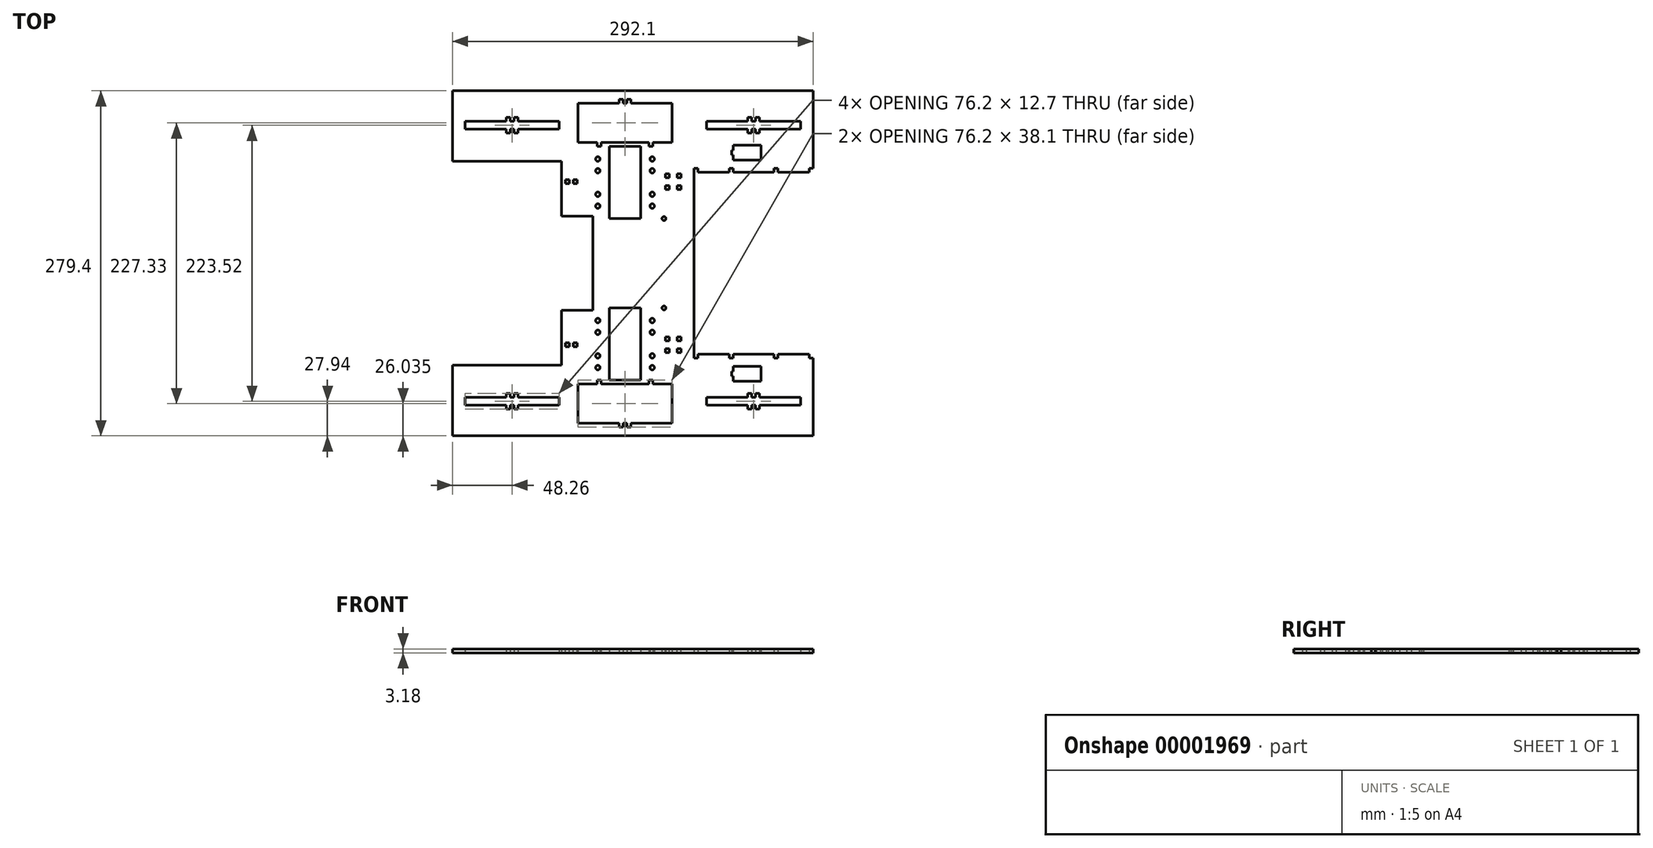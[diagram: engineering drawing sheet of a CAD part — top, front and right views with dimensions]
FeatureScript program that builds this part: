
annotation { "Feature Type Name" : "Feature", "Feature Type Description" : "" }
export const myFeature = defineFeature(function(context is Context, id is Id, definition is map)
    precondition{}
    {
        {
            var Q0;
            Q0=qCreatedBy(makeId("Top.planeOp"),FACE);
            var sketch = newSketch(context, id + "F0", { "sketchPlane" : qUnion([Q0])});
            skLineSegment(sketch, "E0.rect.bottom", {"start": v(152.4, -152.4) * mm, "end": v(-152.4, -152.4) * mm, "construction": true});
            skLineSegment(sketch, "E0.rect.top", {"start": v(152.4, 152.4) * mm, "end": v(-152.4, 152.4) * mm, "construction": true});
            skLineSegment(sketch, "E0.rect.left", {"start": v(152.4, -152.4) * mm, "end": v(152.4, 152.4) * mm, "construction": true});
            skLineSegment(sketch, "E0.rect.right", {"start": v(-152.4, -152.4) * mm, "end": v(-152.4, 152.4) * mm, "construction": true});
            skLineSegment(sketch, "E1.rect.left", {"start": v(55.88, -73.66) * mm, "end": v(55.88, 73.66) * mm});
            skLineSegment(sketch, "E2", {"start": v(152.4, 73.66) * mm, "end": v(152.4, 139.7) * mm});
            skLineSegment(sketch, "E3", {"start": v(152.4, 139.7) * mm, "end": v(-139.7, 139.7) * mm});
            skLineSegment(sketch, "E4", {"start": v(152.4, -73.66) * mm, "end": v(152.4, -139.7) * mm});
            skLineSegment(sketch, "E5", {"start": v(152.4, -139.7) * mm, "end": v(-139.7, -139.7) * mm});
            skLineSegment(sketch, "E6.rect.bottom", {"start": v(38.1, 97.8) * mm, "end": v(22.5, 97.8) * mm});
            skLineSegment(sketch, "E6.rect.top", {"start": v(38.1, 129.54) * mm, "end": v(4.76, 129.54) * mm});
            skLineSegment(sketch, "E6.rect.left", {"start": v(38.1, 97.8) * mm, "end": v(38.1, 129.54) * mm});
            skLineSegment(sketch, "E6.rect.right", {"start": v(-38.1, 97.8) * mm, "end": v(-38.1, 129.54) * mm});
            skPoint(sketch, "E6.rect.middle", {"position": v(0, 113.67) * mm});
            skLineSegment(sketch, "E7", {"start": v(55.88, 0) * mm, "end": v(-60.71, 0) * mm, "construction": true});
            skLineSegment(sketch, "E8.rect.bottom", {"start": v(12.7, 94.62) * mm, "end": v(-12.7, 94.62) * mm});
            skLineSegment(sketch, "E8.rect.top", {"start": v(12.7, 36.2) * mm, "end": v(-12.7, 36.2) * mm});
            skLineSegment(sketch, "E8.rect.left", {"start": v(12.7, 94.62) * mm, "end": v(12.7, 36.2) * mm});
            skLineSegment(sketch, "E8.rect.right", {"start": v(-12.7, 94.62) * mm, "end": v(-12.7, 36.2) * mm});
            skPoint(sketch, "E8.rect.middle", {"position": v(0, 65.4) * mm});
            skPoint(sketch, "E9.0.MirrorP", {"position": v(0, -65.4) * mm});
            skLineSegment(sketch, "E9.1.MirrorCS", {"start": v(12.7, -36.2) * mm, "end": v(-12.7, -36.2) * mm});
            skLineSegment(sketch, "E10.0.MirrorCS", {"start": v(-12.7, -94.62) * mm, "end": v(-12.7, -36.2) * mm});
            skLineSegment(sketch, "E11.0.MirrorCS", {"start": v(12.7, -94.62) * mm, "end": v(12.7, -36.2) * mm});
            skLineSegment(sketch, "E12.0.MirrorCS", {"start": v(12.7, -94.62) * mm, "end": v(-12.7, -94.62) * mm});
            skLineSegment(sketch, "E13.rect.bottom", {"start": v(136.62, -75.38) * mm, "end": v(73.12, -75.38) * mm, "construction": true});
            skLineSegment(sketch, "E13.rect.top", {"start": v(136.62, -138.88) * mm, "end": v(73.12, -138.88) * mm, "construction": true});
            skLineSegment(sketch, "E13.rect.left", {"start": v(136.62, -75.38) * mm, "end": v(136.62, -138.88) * mm, "construction": true});
            skLineSegment(sketch, "E13.rect.right", {"start": v(73.12, -75.38) * mm, "end": v(73.12, -138.88) * mm, "construction": true});
            skPoint(sketch, "E13.rect.middle", {"position": v(104.87, -107.13) * mm});
            skLineSegment(sketch, "E14", {"start": v(-139.7, 94.62) * mm, "end": v(-139.7, 139.7) * mm});
            skLineSegment(sketch, "E15.0.MirrorCS", {"start": v(-139.7, -94.62) * mm, "end": v(-139.7, -139.7) * mm});
            skLineSegment(sketch, "E16", {"start": v(-139.7, 94.62) * mm, "end": v(-139.7, 82.55) * mm});
            skLineSegment(sketch, "E17.0.MirrorCS", {"start": v(-139.7, -94.62) * mm, "end": v(-139.7, -82.55) * mm});
            skLineSegment(sketch, "E18", {"start": v(0, 65.4) * mm, "end": v(0, -65.4) * mm, "construction": true});
            skLineSegment(sketch, "E19.bottom", {"start": v(66.04, 114.94) * mm, "end": v(99.38, 114.94) * mm});
            skLineSegment(sketch, "E19.top", {"start": v(66.04, 108.59) * mm, "end": v(99.38, 108.59) * mm});
            skLineSegment(sketch, "E19.left", {"start": v(66.04, 114.94) * mm, "end": v(66.04, 108.59) * mm});
            skLineSegment(sketch, "E19.right", {"start": v(142.24, 114.94) * mm, "end": v(142.24, 108.59) * mm});
            skCircle(sketch, "E20", {"center": v(31.55, 36.2) * mm, "radius": 1.59 * mm});
            skCircle(sketch, "E21.0.MirrorC", {"center": v(31.55, -36.2) * mm, "radius": 1.59 * mm});
            skLineSegment(sketch, "E22", {"start": v(0, 65.4) * mm, "end": v(-22.02, 65.4) * mm, "construction": true});
            skLineSegment(sketch, "E23", {"start": v(-22.02, 74.93) * mm, "end": v(-22.02, 55.88) * mm, "construction": true});
            skLineSegment(sketch, "E24", {"start": v(-22.02, 74.93) * mm, "end": v(-22.02, 84.46) * mm, "construction": true});
            skLineSegment(sketch, "E25", {"start": v(-22.02, 55.88) * mm, "end": v(-22.02, 46.36) * mm, "construction": true});
            skCircle(sketch, "E26", {"center": v(-22.02, 84.46) * mm, "radius": 1.83 * mm});
            skCircle(sketch, "E27", {"center": v(-22.02, 74.93) * mm, "radius": 1.83 * mm});
            skCircle(sketch, "E28", {"center": v(-22.02, 55.88) * mm, "radius": 1.83 * mm});
            skCircle(sketch, "E29", {"center": v(-22.02, 46.36) * mm, "radius": 1.83 * mm});
            skCircle(sketch, "E30.0.MirrorC", {"center": v(22.02, 84.46) * mm, "radius": 1.83 * mm});
            skCircle(sketch, "E31.0.MirrorC", {"center": v(22.02, 74.93) * mm, "radius": 1.83 * mm});
            skCircle(sketch, "E32.0.MirrorC", {"center": v(22.02, 55.88) * mm, "radius": 1.83 * mm});
            skCircle(sketch, "E33.0.MirrorC", {"center": v(22.02, 46.36) * mm, "radius": 1.83 * mm});
            skCircle(sketch, "E34.0.MirrorC", {"center": v(22.02, -74.93) * mm, "radius": 1.83 * mm});
            skCircle(sketch, "E34.1.MirrorC", {"center": v(22.02, -46.36) * mm, "radius": 1.83 * mm});
            skCircle(sketch, "E34.2.MirrorC", {"center": v(22.02, -55.88) * mm, "radius": 1.83 * mm});
            skCircle(sketch, "E34.3.MirrorC", {"center": v(22.02, -84.46) * mm, "radius": 1.83 * mm});
            skCircle(sketch, "E35.0.MirrorC", {"center": v(-22.02, -46.36) * mm, "radius": 1.83 * mm});
            skCircle(sketch, "E36.0.MirrorC", {"center": v(-22.02, -55.88) * mm, "radius": 1.83 * mm});
            skCircle(sketch, "E37.0.MirrorC", {"center": v(-22.02, -74.93) * mm, "radius": 1.83 * mm});
            skCircle(sketch, "E38.0.MirrorC", {"center": v(-22.02, -84.46) * mm, "radius": 1.83 * mm});
            skLineSegment(sketch, "E39.0.MirrorCS", {"start": v(-89.85, 108.59) * mm, "end": v(-93.03, 108.59) * mm});
            skLineSegment(sketch, "E39.1.MirrorCS", {"start": v(-89.85, 105.4) * mm, "end": v(-86.68, 105.4) * mm});
            skLineSegment(sketch, "E39.2.MirrorCS", {"start": v(-89.85, 108.59) * mm, "end": v(-89.85, 105.4) * mm});
            skLineSegment(sketch, "E39.3.MirrorCS", {"start": v(-93.03, 108.59) * mm, "end": v(-93.03, 105.4) * mm});
            skLineSegment(sketch, "E39.4.MirrorCS", {"start": v(-93.03, 105.4) * mm, "end": v(-96.2, 105.4) * mm});
            skLineSegment(sketch, "E39.5.MirrorCS", {"start": v(-89.85, 118.1) * mm, "end": v(-86.68, 118.1) * mm});
            skLineSegment(sketch, "E39.6.MirrorCS", {"start": v(-96.2, 105.4) * mm, "end": v(-96.2, 108.59) * mm});
            skLineSegment(sketch, "E39.7.MirrorCS", {"start": v(-93.03, 118.1) * mm, "end": v(-93.03, 114.93) * mm});
            skLineSegment(sketch, "E39.8.MirrorCS", {"start": v(-89.85, 114.93) * mm, "end": v(-93.03, 114.93) * mm});
            skLineSegment(sketch, "E39.9.MirrorCS", {"start": v(-96.2, 114.93) * mm, "end": v(-96.2, 118.1) * mm});
            skLineSegment(sketch, "E39.10.MirrorCS", {"start": v(-96.2, 118.1) * mm, "end": v(-93.03, 118.1) * mm});
            skLineSegment(sketch, "E39.11.MirrorCS", {"start": v(-89.85, 114.93) * mm, "end": v(-89.85, 118.1) * mm});
            skLineSegment(sketch, "E39.12.MirrorCS", {"start": v(-86.68, 118.1) * mm, "end": v(-86.68, 114.93) * mm});
            skLineSegment(sketch, "E39.13.MirrorCS", {"start": v(-86.68, 105.4) * mm, "end": v(-86.68, 108.58) * mm});
            skLineSegment(sketch, "E39.15.MirrorCS", {"start": v(-96.2, 108.59) * mm, "end": v(-129.54, 108.59) * mm});
            skLineSegment(sketch, "E39.16.MirrorCS", {"start": v(-53.34, 114.93) * mm, "end": v(-86.68, 114.93) * mm});
            skLineSegment(sketch, "E39.17.MirrorCS", {"start": v(-96.2, 114.93) * mm, "end": v(-129.54, 114.93) * mm});
            skLineSegment(sketch, "E39.18.MirrorCS", {"start": v(-53.34, 108.59) * mm, "end": v(-86.68, 108.59) * mm});
            skLineSegment(sketch, "E39.19.MirrorCS", {"start": v(-53.34, 114.93) * mm, "end": v(-53.34, 108.58) * mm});
            skLineSegment(sketch, "E39.21.MirrorCS", {"start": v(-129.54, 114.94) * mm, "end": v(-129.54, 108.59) * mm});
            skPoint(sketch, "E40", {"position": v(104.14, 114.94) * mm});
            skLineSegment(sketch, "E41.rect.bottom", {"start": v(105.73, 114.94) * mm, "end": v(102.55, 114.94) * mm});
            skLineSegment(sketch, "E41.rect.left", {"start": v(105.73, 114.94) * mm, "end": v(105.73, 118.11) * mm});
            skLineSegment(sketch, "E41.rect.right", {"start": v(102.55, 114.94) * mm, "end": v(102.55, 118.11) * mm});
            skPoint(sketch, "E41.rect.middle", {"position": v(104.14, 116.52) * mm});
            skLineSegment(sketch, "E42", {"start": v(102.55, 118.11) * mm, "end": v(99.38, 118.11) * mm});
            skLineSegment(sketch, "E43", {"start": v(99.38, 118.11) * mm, "end": v(99.38, 114.94) * mm});
            skLineSegment(sketch, "E44", {"start": v(105.73, 118.11) * mm, "end": v(108.9, 118.11) * mm});
            skLineSegment(sketch, "E45", {"start": v(108.9, 118.11) * mm, "end": v(108.9, 114.94) * mm});
            skLineSegment(sketch, "E46.trimOffspring", {"start": v(102.55, 114.94) * mm, "end": v(105.73, 114.94) * mm});
            skLineSegment(sketch, "E47.trimOffspring", {"start": v(108.9, 114.94) * mm, "end": v(142.24, 114.94) * mm});
            skLineSegment(sketch, "E48", {"start": v(99.38, 108.59) * mm, "end": v(99.38, 105.41) * mm});
            skLineSegment(sketch, "E49", {"start": v(99.38, 105.41) * mm, "end": v(102.55, 105.41) * mm});
            skLineSegment(sketch, "E50", {"start": v(102.55, 105.41) * mm, "end": v(102.55, 108.59) * mm});
            skLineSegment(sketch, "E51", {"start": v(105.73, 108.59) * mm, "end": v(105.73, 105.41) * mm});
            skLineSegment(sketch, "E52", {"start": v(105.73, 105.41) * mm, "end": v(108.9, 105.41) * mm});
            skLineSegment(sketch, "E53", {"start": v(108.9, 105.41) * mm, "end": v(108.9, 108.59) * mm});
            skLineSegment(sketch, "E54.trimOffspring", {"start": v(102.55, 108.59) * mm, "end": v(105.73, 108.59) * mm});
            skLineSegment(sketch, "E55.trimOffspring", {"start": v(108.9, 108.59) * mm, "end": v(142.24, 108.59) * mm});
            skLineSegment(sketch, "E56.0.MirrorCS", {"start": v(102.55, -114.94) * mm, "end": v(105.73, -114.94) * mm});
            skLineSegment(sketch, "E56.1.MirrorCS", {"start": v(105.73, -114.94) * mm, "end": v(102.55, -114.94) * mm});
            skLineSegment(sketch, "E56.2.MirrorCS", {"start": v(102.55, -114.94) * mm, "end": v(102.55, -118.11) * mm});
            skLineSegment(sketch, "E56.3.MirrorCS", {"start": v(102.55, -118.11) * mm, "end": v(99.38, -118.11) * mm});
            skLineSegment(sketch, "E56.4.MirrorCS", {"start": v(108.9, -105.41) * mm, "end": v(108.9, -108.59) * mm});
            skLineSegment(sketch, "E56.5.MirrorCS", {"start": v(105.73, -118.11) * mm, "end": v(108.9, -118.11) * mm});
            skLineSegment(sketch, "E56.6.MirrorCS", {"start": v(105.73, -114.94) * mm, "end": v(105.73, -118.11) * mm});
            skLineSegment(sketch, "E56.7.MirrorCS", {"start": v(99.38, -105.41) * mm, "end": v(102.55, -105.41) * mm});
            skLineSegment(sketch, "E56.8.MirrorCS", {"start": v(102.55, -108.59) * mm, "end": v(105.73, -108.59) * mm});
            skLineSegment(sketch, "E56.9.MirrorCS", {"start": v(108.9, -118.11) * mm, "end": v(108.9, -114.94) * mm});
            skLineSegment(sketch, "E56.10.MirrorCS", {"start": v(105.73, -108.59) * mm, "end": v(105.73, -105.41) * mm});
            skLineSegment(sketch, "E56.11.MirrorCS", {"start": v(105.73, -105.41) * mm, "end": v(108.9, -105.41) * mm});
            skLineSegment(sketch, "E56.12.MirrorCS", {"start": v(99.38, -108.59) * mm, "end": v(99.38, -105.41) * mm});
            skLineSegment(sketch, "E56.13.MirrorCS", {"start": v(99.38, -118.11) * mm, "end": v(99.38, -114.94) * mm});
            skLineSegment(sketch, "E56.14.MirrorCS", {"start": v(102.55, -105.41) * mm, "end": v(102.55, -108.59) * mm});
            skLineSegment(sketch, "E56.15.MirrorCS", {"start": v(142.24, -114.94) * mm, "end": v(142.24, -108.59) * mm});
            skLineSegment(sketch, "E56.16.MirrorCS", {"start": v(108.9, -108.59) * mm, "end": v(142.24, -108.59) * mm});
            skLineSegment(sketch, "E56.17.MirrorCS", {"start": v(66.04, -114.94) * mm, "end": v(66.04, -108.59) * mm});
            skLineSegment(sketch, "E56.18.MirrorCS", {"start": v(66.04, -114.94) * mm, "end": v(99.38, -114.94) * mm});
            skLineSegment(sketch, "E56.19.MirrorCS", {"start": v(108.9, -114.94) * mm, "end": v(142.24, -114.94) * mm});
            skLineSegment(sketch, "E56.20.MirrorCS", {"start": v(66.04, -108.59) * mm, "end": v(99.38, -108.59) * mm});
            skPoint(sketch, "E56.21.MirrorP", {"position": v(104.14, -114.94) * mm});
            skPoint(sketch, "E56.22.MirrorP", {"position": v(104.14, -116.52) * mm});
            skLineSegment(sketch, "E57.rect.bottom", {"start": v(1.59, 129.54) * mm, "end": v(-1.59, 129.54) * mm});
            skLineSegment(sketch, "E57.rect.left", {"start": v(1.59, 129.54) * mm, "end": v(1.59, 132.72) * mm});
            skLineSegment(sketch, "E57.rect.right", {"start": v(-1.59, 129.54) * mm, "end": v(-1.59, 132.72) * mm});
            skPoint(sketch, "E57.rect.middle", {"position": v(0, 131.13) * mm});
            skLineSegment(sketch, "E58", {"start": v(1.59, 132.72) * mm, "end": v(4.76, 132.72) * mm});
            skLineSegment(sketch, "E59", {"start": v(4.76, 132.72) * mm, "end": v(4.76, 129.54) * mm});
            skLineSegment(sketch, "E60", {"start": v(-1.59, 132.72) * mm, "end": v(-4.76, 132.72) * mm});
            skLineSegment(sketch, "E61", {"start": v(-4.76, 132.72) * mm, "end": v(-4.76, 129.54) * mm});
            skLineSegment(sketch, "E62.trimOffspring", {"start": v(-4.76, 129.54) * mm, "end": v(-38.1, 129.54) * mm});
            skLineSegment(sketch, "E63", {"start": v(-19.33, 97.8) * mm, "end": v(-19.33, 94.62) * mm});
            skLineSegment(sketch, "E64", {"start": v(-19.33, 94.62) * mm, "end": v(-22.5, 94.62) * mm});
            skLineSegment(sketch, "E65", {"start": v(-22.5, 94.62) * mm, "end": v(-22.5, 97.8) * mm});
            skLineSegment(sketch, "E66.0.MirrorCS", {"start": v(22.5, 94.62) * mm, "end": v(22.5, 97.8) * mm});
            skLineSegment(sketch, "E66.1.MirrorCS", {"start": v(19.33, 94.62) * mm, "end": v(22.5, 94.62) * mm});
            skLineSegment(sketch, "E66.2.MirrorCS", {"start": v(19.33, 97.8) * mm, "end": v(19.33, 94.62) * mm});
            skLineSegment(sketch, "E67.trimOffspring", {"start": v(-22.5, 97.8) * mm, "end": v(-38.1, 97.8) * mm});
            skLineSegment(sketch, "E68.trimOffspring", {"start": v(19.33, 97.8) * mm, "end": v(-19.33, 97.8) * mm});
            skLineSegment(sketch, "E69.0.MirrorCS", {"start": v(1.59, -129.54) * mm, "end": v(-1.59, -129.54) * mm});
            skLineSegment(sketch, "E69.1.MirrorCS", {"start": v(1.59, -129.54) * mm, "end": v(1.59, -132.72) * mm});
            skLineSegment(sketch, "E69.2.MirrorCS", {"start": v(-1.59, -129.54) * mm, "end": v(-1.59, -132.72) * mm});
            skLineSegment(sketch, "E69.3.MirrorCS", {"start": v(1.59, -129.54) * mm, "end": v(-1.59, -129.54) * mm});
            skLineSegment(sketch, "E69.4.MirrorCS", {"start": v(-1.59, -132.72) * mm, "end": v(-4.76, -132.72) * mm});
            skLineSegment(sketch, "E69.5.MirrorCS", {"start": v(4.76, -132.72) * mm, "end": v(4.76, -129.54) * mm});
            skPoint(sketch, "E69.6.MirrorP", {"position": v(0, -131.13) * mm});
            skLineSegment(sketch, "E69.7.MirrorCS", {"start": v(1.59, -132.72) * mm, "end": v(4.76, -132.72) * mm});
            skLineSegment(sketch, "E69.8.MirrorCS", {"start": v(-4.76, -132.72) * mm, "end": v(-4.76, -129.54) * mm});
            skLineSegment(sketch, "E69.9.MirrorCS", {"start": v(-4.76, -129.54) * mm, "end": v(-38.1, -129.54) * mm});
            skPoint(sketch, "E69.10.MirrorP", {"position": v(0, -113.67) * mm});
            skLineSegment(sketch, "E69.11.MirrorCS", {"start": v(19.33, -94.62) * mm, "end": v(22.5, -94.62) * mm});
            skLineSegment(sketch, "E69.12.MirrorCS", {"start": v(19.33, -97.8) * mm, "end": v(19.33, -94.62) * mm});
            skLineSegment(sketch, "E69.13.MirrorCS", {"start": v(22.5, -94.62) * mm, "end": v(22.5, -97.8) * mm});
            skLineSegment(sketch, "E69.14.MirrorCS", {"start": v(38.1, -129.54) * mm, "end": v(4.76, -129.54) * mm});
            skLineSegment(sketch, "E69.15.MirrorCS", {"start": v(38.1, -97.8) * mm, "end": v(22.5, -97.8) * mm});
            skLineSegment(sketch, "E69.16.MirrorCS", {"start": v(19.33, -97.8) * mm, "end": v(-19.33, -97.8) * mm});
            skLineSegment(sketch, "E69.17.MirrorCS", {"start": v(38.1, -97.8) * mm, "end": v(38.1, -129.54) * mm});
            skLineSegment(sketch, "E69.18.MirrorCS", {"start": v(-19.33, -94.62) * mm, "end": v(-22.5, -94.62) * mm});
            skLineSegment(sketch, "E69.19.MirrorCS", {"start": v(-22.5, -94.62) * mm, "end": v(-22.5, -97.8) * mm});
            skLineSegment(sketch, "E69.20.MirrorCS", {"start": v(-19.33, -97.8) * mm, "end": v(-19.33, -94.62) * mm});
            skLineSegment(sketch, "E69.21.MirrorCS", {"start": v(-22.5, -97.8) * mm, "end": v(-38.1, -97.8) * mm});
            skLineSegment(sketch, "E69.22.MirrorCS", {"start": v(-38.1, -97.8) * mm, "end": v(-38.1, -129.54) * mm});
            skLineSegment(sketch, "E70", {"start": v(110.08, 83.44) * mm, "end": v(110.08, 95.63) * mm});
            skLineSegment(sketch, "E71", {"start": v(110.08, 95.63) * mm, "end": v(87.6, 95.63) * mm});
            skLineSegment(sketch, "E72", {"start": v(87.6, 95.63) * mm, "end": v(87.6, 91.44) * mm});
            skLineSegment(sketch, "E73", {"start": v(87.6, 89.53) * mm, "end": v(110.08, 89.53) * mm, "construction": true});
            skPoint(sketch, "E74", {"position": v(104.14, 89.53) * mm});
            skLineSegment(sketch, "E75", {"start": v(149.22, 73.66) * mm, "end": v(123.82, 73.66) * mm});
            skLineSegment(sketch, "E76", {"start": v(110.08, 83.44) * mm, "end": v(87.6, 83.44) * mm});
            skLineSegment(sketch, "E77", {"start": v(104.14, 89.53) * mm, "end": v(104.14, 105.41) * mm, "construction": true});
            skLineSegment(sketch, "E78", {"start": v(104.14, 89.53) * mm, "end": v(104.14, 73.66) * mm, "construction": true});
            skLineSegment(sketch, "E79", {"start": v(87.6, 91.44) * mm, "end": v(86.33, 91.44) * mm});
            skLineSegment(sketch, "E80", {"start": v(86.33, 91.44) * mm, "end": v(86.33, 89.53) * mm});
            skLineSegment(sketch, "E81", {"start": v(86.33, 87.63) * mm, "end": v(87.6, 87.63) * mm});
            skLineSegment(sketch, "E82", {"start": v(87.6, 87.63) * mm, "end": v(87.6, 83.44) * mm});
            skLineSegment(sketch, "E83", {"start": v(87.6, 91.44) * mm, "end": v(87.6, 87.63) * mm, "construction": true});
            skLineSegment(sketch, "E84", {"start": v(86.33, 89.53) * mm, "end": v(86.33, 87.63) * mm});
            skLineSegment(sketch, "E85.0.MirrorCS", {"start": v(110.08, -95.63) * mm, "end": v(87.6, -95.63) * mm});
            skLineSegment(sketch, "E86.0.MirrorCS", {"start": v(110.08, -83.44) * mm, "end": v(110.08, -95.63) * mm});
            skLineSegment(sketch, "E87.0.MirrorCS", {"start": v(110.08, -83.44) * mm, "end": v(87.6, -83.44) * mm});
            skLineSegment(sketch, "E88.0.MirrorCS", {"start": v(87.6, -87.63) * mm, "end": v(87.6, -83.44) * mm});
            skLineSegment(sketch, "E89.0.MirrorCS", {"start": v(86.33, -87.63) * mm, "end": v(87.6, -87.63) * mm});
            skLineSegment(sketch, "E90.0.MirrorCS", {"start": v(86.33, -89.53) * mm, "end": v(86.33, -87.63) * mm});
            skLineSegment(sketch, "E91.0.MirrorCS", {"start": v(86.33, -91.44) * mm, "end": v(86.33, -89.53) * mm});
            skLineSegment(sketch, "E92.0.MirrorCS", {"start": v(87.6, -91.44) * mm, "end": v(86.33, -91.44) * mm});
            skLineSegment(sketch, "E93.0.MirrorCS", {"start": v(87.6, -95.63) * mm, "end": v(87.6, -91.44) * mm});
            skLineSegment(sketch, "E94", {"start": v(55.88, 73.66) * mm, "end": v(55.88, 76.83) * mm});
            skLineSegment(sketch, "E95", {"start": v(55.88, 76.83) * mm, "end": v(59.06, 76.83) * mm});
            skLineSegment(sketch, "E96", {"start": v(59.06, 76.83) * mm, "end": v(59.06, 73.66) * mm});
            skLineSegment(sketch, "E97", {"start": v(149.22, 73.66) * mm, "end": v(149.22, 76.83) * mm});
            skLineSegment(sketch, "E98", {"start": v(149.22, 76.83) * mm, "end": v(152.4, 76.83) * mm});
            skLineSegment(sketch, "E99", {"start": v(123.82, 73.66) * mm, "end": v(123.82, 76.83) * mm});
            skLineSegment(sketch, "E100", {"start": v(123.82, 76.83) * mm, "end": v(120.65, 76.83) * mm});
            skLineSegment(sketch, "E101", {"start": v(120.65, 76.83) * mm, "end": v(120.65, 73.66) * mm});
            skLineSegment(sketch, "E102", {"start": v(84.45, 73.66) * mm, "end": v(84.45, 76.83) * mm});
            skLineSegment(sketch, "E103", {"start": v(84.45, 76.83) * mm, "end": v(87.63, 76.83) * mm});
            skLineSegment(sketch, "E104", {"start": v(87.63, 76.83) * mm, "end": v(87.63, 73.66) * mm});
            skLineSegment(sketch, "E105.trimOffspring", {"start": v(84.45, 73.66) * mm, "end": v(59.05, 73.66) * mm});
            skLineSegment(sketch, "E106.trimOffspring", {"start": v(120.65, 73.66) * mm, "end": v(87.63, 73.66) * mm});
            skLineSegment(sketch, "E107.0.MirrorCS", {"start": v(55.88, -73.66) * mm, "end": v(55.88, -76.83) * mm});
            skLineSegment(sketch, "E107.1.MirrorCS", {"start": v(55.88, -76.83) * mm, "end": v(59.06, -76.83) * mm});
            skLineSegment(sketch, "E107.2.MirrorCS", {"start": v(120.65, -76.83) * mm, "end": v(120.65, -73.66) * mm});
            skLineSegment(sketch, "E107.3.MirrorCS", {"start": v(123.83, -73.66) * mm, "end": v(123.83, -76.83) * mm});
            skLineSegment(sketch, "E107.4.MirrorCS", {"start": v(123.83, -76.83) * mm, "end": v(120.65, -76.83) * mm});
            skLineSegment(sketch, "E107.5.MirrorCS", {"start": v(59.06, -76.83) * mm, "end": v(59.06, -73.66) * mm});
            skLineSegment(sketch, "E107.6.MirrorCS", {"start": v(149.23, -73.66) * mm, "end": v(149.23, -76.83) * mm});
            skLineSegment(sketch, "E107.7.MirrorCS", {"start": v(87.63, -76.83) * mm, "end": v(87.63, -73.66) * mm});
            skLineSegment(sketch, "E107.8.MirrorCS", {"start": v(84.46, -76.83) * mm, "end": v(87.63, -76.83) * mm});
            skLineSegment(sketch, "E107.9.MirrorCS", {"start": v(84.46, -73.66) * mm, "end": v(84.46, -76.83) * mm});
            skLineSegment(sketch, "E107.10.MirrorCS", {"start": v(149.23, -76.83) * mm, "end": v(152.4, -76.83) * mm});
            skLineSegment(sketch, "E107.11.MirrorCS", {"start": v(149.23, -73.66) * mm, "end": v(123.83, -73.66) * mm});
            skLineSegment(sketch, "E107.12.MirrorCS", {"start": v(84.46, -73.66) * mm, "end": v(59.06, -73.66) * mm});
            skLineSegment(sketch, "E107.13.MirrorCS", {"start": v(120.65, -73.66) * mm, "end": v(87.63, -73.66) * mm});
            skLineSegment(sketch, "E108", {"start": v(-139.7, 82.55) * mm, "end": v(-51.59, 82.55) * mm});
            skLineSegment(sketch, "E109", {"start": v(-51.59, 82.55) * mm, "end": v(-51.59, 38.1) * mm});
            skLineSegment(sketch, "E110", {"start": v(-51.59, -82.55) * mm, "end": v(-139.7, -82.55) * mm});
            skLineSegment(sketch, "E111", {"start": v(-51.59, -38.1) * mm, "end": v(-26.19, -38.1) * mm});
            skLineSegment(sketch, "E112", {"start": v(-26.19, -38.1) * mm, "end": v(-26.19, 0) * mm});
            skLineSegment(sketch, "E113.0.MirrorCS", {"start": v(-26.19, 38.1) * mm, "end": v(-26.19, 0) * mm});
            skLineSegment(sketch, "E114.0.MirrorCS", {"start": v(-51.59, 38.1) * mm, "end": v(-26.19, 38.1) * mm});
            skLineSegment(sketch, "E115.trimOffspring", {"start": v(-51.59, -38.1) * mm, "end": v(-51.59, -82.55) * mm});
            skLineSegment(sketch, "E116.0.MirrorCS", {"start": v(-89.85, -108.59) * mm, "end": v(-89.85, -105.4) * mm});
            skLineSegment(sketch, "E116.1.MirrorCS", {"start": v(-86.68, -118.1) * mm, "end": v(-86.68, -114.93) * mm});
            skLineSegment(sketch, "E116.2.MirrorCS", {"start": v(-93.03, -105.4) * mm, "end": v(-96.2, -105.4) * mm});
            skLineSegment(sketch, "E116.3.MirrorCS", {"start": v(-89.85, -108.59) * mm, "end": v(-93.03, -108.59) * mm});
            skLineSegment(sketch, "E116.4.MirrorCS", {"start": v(-129.54, -114.94) * mm, "end": v(-129.54, -108.59) * mm});
            skLineSegment(sketch, "E116.5.MirrorCS", {"start": v(-93.03, -108.59) * mm, "end": v(-93.03, -105.4) * mm});
            skLineSegment(sketch, "E116.6.MirrorCS", {"start": v(-96.2, -114.93) * mm, "end": v(-96.2, -118.1) * mm});
            skLineSegment(sketch, "E116.7.MirrorCS", {"start": v(-96.2, -118.1) * mm, "end": v(-93.03, -118.1) * mm});
            skLineSegment(sketch, "E116.8.MirrorCS", {"start": v(-89.85, -105.4) * mm, "end": v(-86.68, -105.4) * mm});
            skLineSegment(sketch, "E116.9.MirrorCS", {"start": v(-93.03, -118.1) * mm, "end": v(-93.03, -114.93) * mm});
            skLineSegment(sketch, "E116.10.MirrorCS", {"start": v(-96.2, -105.4) * mm, "end": v(-96.2, -108.59) * mm});
            skLineSegment(sketch, "E116.11.MirrorCS", {"start": v(-86.68, -105.4) * mm, "end": v(-86.68, -108.58) * mm});
            skLineSegment(sketch, "E116.12.MirrorCS", {"start": v(-53.34, -114.93) * mm, "end": v(-53.34, -108.58) * mm});
            skLineSegment(sketch, "E116.13.MirrorCS", {"start": v(-89.85, -118.1) * mm, "end": v(-86.68, -118.1) * mm});
            skLineSegment(sketch, "E116.14.MirrorCS", {"start": v(-89.85, -114.93) * mm, "end": v(-89.85, -118.1) * mm});
            skLineSegment(sketch, "E116.15.MirrorCS", {"start": v(-89.85, -114.93) * mm, "end": v(-93.03, -114.93) * mm});
            skLineSegment(sketch, "E116.16.MirrorCS", {"start": v(-96.2, -114.93) * mm, "end": v(-129.54, -114.93) * mm});
            skLineSegment(sketch, "E116.17.MirrorCS", {"start": v(-53.34, -108.58) * mm, "end": v(-86.68, -108.59) * mm});
            skLineSegment(sketch, "E116.18.MirrorCS", {"start": v(-96.2, -108.59) * mm, "end": v(-129.54, -108.59) * mm});
            skLineSegment(sketch, "E116.19.MirrorCS", {"start": v(-53.34, -114.93) * mm, "end": v(-86.68, -114.93) * mm});
            skSolve(sketch);
        }
        {
            var Q0;
            {var subQ2=sQuery(id+"F0.wireOp",EDGE,"E3");Q0=makeQuery(id+"F0.imprint","IMPRINT",FACE,{"disambiguationData":[TD([[makeQuery(id+"F0.imprint","IMPRINT",EDGE,{"derivedFrom":subQ2}),1.0]])]});}
            extrude(context, id + "F1", {"entities" : qUnion([Q0]), "depth" : 3.17 * mm});
        }
        {
            var Q0;
            Q0=makeQuery(id+"F1.opExtrude","CAP_FACE",FACE,{"disambiguationData":[OSD([sQuery(id+"F0.wireOp",EDGE,"E2"),sQuery(id+"F0.wireOp",EDGE,"E3"),sQuery(id+"F0.wireOp",EDGE,"E4"),sQuery(id+"F0.wireOp",EDGE,"E5"),sQuery(id+"F0.wireOp",EDGE,"E6.rect.bottom"),sQuery(id+"F0.wireOp",EDGE,"E6.rect.top"),sQuery(id+"F0.wireOp",EDGE,"E6.rect.left"),sQuery(id+"F0.wireOp",EDGE,"E6.rect.right"),sQuery(id+"F0.wireOp",EDGE,"E8.rect.bottom"),sQuery(id+"F0.wireOp",EDGE,"E8.rect.top"),sQuery(id+"F0.wireOp",EDGE,"E8.rect.left"),sQuery(id+"F0.wireOp",EDGE,"E8.rect.right"),sQuery(id+"F0.wireOp",EDGE,"E9.1.MirrorCS"),sQuery(id+"F0.wireOp",EDGE,"E10.0.MirrorCS"),sQuery(id+"F0.wireOp",EDGE,"E11.0.MirrorCS"),sQuery(id+"F0.wireOp",EDGE,"E12.0.MirrorCS"),sQuery(id+"F0.wireOp",EDGE,"E14"),sQuery(id+"F0.wireOp",EDGE,"E17.0.MirrorCS"),sQuery(id+"F0.wireOp",EDGE,"E19.bottom"),sQuery(id+"F0.wireOp",EDGE,"E19.top"),sQuery(id+"F0.wireOp",EDGE,"E19.left"),sQuery(id+"F0.wireOp",EDGE,"E19.right"),sQuery(id+"F0.wireOp",EDGE,"E20"),sQuery(id+"F0.wireOp",EDGE,"E21.0.MirrorC"),sQuery(id+"F0.wireOp",EDGE,"E26"),sQuery(id+"F0.wireOp",EDGE,"E27"),sQuery(id+"F0.wireOp",EDGE,"E28"),sQuery(id+"F0.wireOp",EDGE,"E29"),sQuery(id+"F0.wireOp",EDGE,"E30.0.MirrorC"),sQuery(id+"F0.wireOp",EDGE,"E31.0.MirrorC"),sQuery(id+"F0.wireOp",EDGE,"E32.0.MirrorC"),sQuery(id+"F0.wireOp",EDGE,"E33.0.MirrorC"),sQuery(id+"F0.wireOp",EDGE,"E34.0.MirrorC"),sQuery(id+"F0.wireOp",EDGE,"E34.1.MirrorC"),sQuery(id+"F0.wireOp",EDGE,"E34.2.MirrorC"),sQuery(id+"F0.wireOp",EDGE,"E34.3.MirrorC"),sQuery(id+"F0.wireOp",EDGE,"E35.0.MirrorC"),sQuery(id+"F0.wireOp",EDGE,"E36.0.MirrorC"),sQuery(id+"F0.wireOp",EDGE,"E37.0.MirrorC"),sQuery(id+"F0.wireOp",EDGE,"E38.0.MirrorC"),sQuery(id+"F0.wireOp",EDGE,"E39.0.MirrorCS"),sQuery(id+"F0.wireOp",EDGE,"E39.1.MirrorCS"),sQuery(id+"F0.wireOp",EDGE,"E39.2.MirrorCS"),sQuery(id+"F0.wireOp",EDGE,"E39.3.MirrorCS"),sQuery(id+"F0.wireOp",EDGE,"E39.4.MirrorCS"),sQuery(id+"F0.wireOp",EDGE,"E39.5.MirrorCS"),sQuery(id+"F0.wireOp",EDGE,"E39.6.MirrorCS"),sQuery(id+"F0.wireOp",EDGE,"E39.7.MirrorCS"),sQuery(id+"F0.wireOp",EDGE,"E39.8.MirrorCS"),sQuery(id+"F0.wireOp",EDGE,"E39.9.MirrorCS"),sQuery(id+"F0.wireOp",EDGE,"E39.10.MirrorCS"),sQuery(id+"F0.wireOp",EDGE,"E39.11.MirrorCS"),sQuery(id+"F0.wireOp",EDGE,"E39.12.MirrorCS"),sQuery(id+"F0.wireOp",EDGE,"E39.13.MirrorCS"),sQuery(id+"F0.wireOp",EDGE,"E39.15.MirrorCS"),sQuery(id+"F0.wireOp",EDGE,"E39.16.MirrorCS"),sQuery(id+"F0.wireOp",EDGE,"E39.17.MirrorCS"),sQuery(id+"F0.wireOp",EDGE,"E39.18.MirrorCS"),sQuery(id+"F0.wireOp",EDGE,"E39.19.MirrorCS"),sQuery(id+"F0.wireOp",EDGE,"E39.21.MirrorCS"),sQuery(id+"F0.wireOp",EDGE,"E41.rect.left"),sQuery(id+"F0.wireOp",EDGE,"E41.rect.right"),sQuery(id+"F0.wireOp",EDGE,"E42"),sQuery(id+"F0.wireOp",EDGE,"E43"),sQuery(id+"F0.wireOp",EDGE,"E44"),sQuery(id+"F0.wireOp",EDGE,"E45"),sQuery(id+"F0.wireOp",EDGE,"E46.trimOffspring"),sQuery(id+"F0.wireOp",EDGE,"E47.trimOffspring"),sQuery(id+"F0.wireOp",EDGE,"E48"),sQuery(id+"F0.wireOp",EDGE,"E49"),sQuery(id+"F0.wireOp",EDGE,"E50"),sQuery(id+"F0.wireOp",EDGE,"E51"),sQuery(id+"F0.wireOp",EDGE,"E52"),sQuery(id+"F0.wireOp",EDGE,"E53"),sQuery(id+"F0.wireOp",EDGE,"E54.trimOffspring"),sQuery(id+"F0.wireOp",EDGE,"E55.trimOffspring"),sQuery(id+"F0.wireOp",EDGE,"E56.1.MirrorCS"),sQuery(id+"F0.wireOp",EDGE,"E56.2.MirrorCS"),sQuery(id+"F0.wireOp",EDGE,"E56.3.MirrorCS"),sQuery(id+"F0.wireOp",EDGE,"E56.4.MirrorCS"),sQuery(id+"F0.wireOp",EDGE,"E56.5.MirrorCS"),sQuery(id+"F0.wireOp",EDGE,"E56.6.MirrorCS"),sQuery(id+"F0.wireOp",EDGE,"E56.7.MirrorCS"),sQuery(id+"F0.wireOp",EDGE,"E56.8.MirrorCS"),sQuery(id+"F0.wireOp",EDGE,"E56.9.MirrorCS"),sQuery(id+"F0.wireOp",EDGE,"E56.10.MirrorCS"),sQuery(id+"F0.wireOp",EDGE,"E56.11.MirrorCS"),sQuery(id+"F0.wireOp",EDGE,"E56.12.MirrorCS"),sQuery(id+"F0.wireOp",EDGE,"E56.13.MirrorCS"),sQuery(id+"F0.wireOp",EDGE,"E56.14.MirrorCS"),sQuery(id+"F0.wireOp",EDGE,"E56.15.MirrorCS"),sQuery(id+"F0.wireOp",EDGE,"E56.16.MirrorCS"),sQuery(id+"F0.wireOp",EDGE,"E56.17.MirrorCS"),sQuery(id+"F0.wireOp",EDGE,"E56.18.MirrorCS"),sQuery(id+"F0.wireOp",EDGE,"E56.19.MirrorCS"),sQuery(id+"F0.wireOp",EDGE,"E56.20.MirrorCS"),sQuery(id+"F0.wireOp",EDGE,"E57.rect.left"),sQuery(id+"F0.wireOp",EDGE,"E57.rect.right"),sQuery(id+"F0.wireOp",EDGE,"E58"),sQuery(id+"F0.wireOp",EDGE,"E59"),sQuery(id+"F0.wireOp",EDGE,"E60"),sQuery(id+"F0.wireOp",EDGE,"E61"),sQuery(id+"F0.wireOp",EDGE,"E62.trimOffspring"),sQuery(id+"F0.wireOp",EDGE,"E57.rect.bottom"),sQuery(id+"F0.wireOp",EDGE,"E63"),sQuery(id+"F0.wireOp",EDGE,"E64"),sQuery(id+"F0.wireOp",EDGE,"E65"),sQuery(id+"F0.wireOp",EDGE,"E66.0.MirrorCS"),sQuery(id+"F0.wireOp",EDGE,"E66.1.MirrorCS"),sQuery(id+"F0.wireOp",EDGE,"E66.2.MirrorCS"),sQuery(id+"F0.wireOp",EDGE,"E67.trimOffspring"),sQuery(id+"F0.wireOp",EDGE,"E68.trimOffspring"),sQuery(id+"F0.wireOp",EDGE,"E69.1.MirrorCS"),sQuery(id+"F0.wireOp",EDGE,"E69.2.MirrorCS"),sQuery(id+"F0.wireOp",EDGE,"E69.3.MirrorCS"),sQuery(id+"F0.wireOp",EDGE,"E69.4.MirrorCS"),sQuery(id+"F0.wireOp",EDGE,"E69.5.MirrorCS"),sQuery(id+"F0.wireOp",EDGE,"E69.7.MirrorCS"),sQuery(id+"F0.wireOp",EDGE,"E69.8.MirrorCS"),sQuery(id+"F0.wireOp",EDGE,"E69.9.MirrorCS"),sQuery(id+"F0.wireOp",EDGE,"E69.11.MirrorCS"),sQuery(id+"F0.wireOp",EDGE,"E69.12.MirrorCS"),sQuery(id+"F0.wireOp",EDGE,"E69.13.MirrorCS"),sQuery(id+"F0.wireOp",EDGE,"E69.14.MirrorCS"),sQuery(id+"F0.wireOp",EDGE,"E69.15.MirrorCS"),sQuery(id+"F0.wireOp",EDGE,"E69.16.MirrorCS"),sQuery(id+"F0.wireOp",EDGE,"E69.17.MirrorCS"),sQuery(id+"F0.wireOp",EDGE,"E69.18.MirrorCS"),sQuery(id+"F0.wireOp",EDGE,"E69.19.MirrorCS"),sQuery(id+"F0.wireOp",EDGE,"E69.20.MirrorCS"),sQuery(id+"F0.wireOp",EDGE,"E69.21.MirrorCS"),sQuery(id+"F0.wireOp",EDGE,"E69.22.MirrorCS"),sQuery(id+"F0.wireOp",EDGE,"E70"),sQuery(id+"F0.wireOp",EDGE,"E71"),sQuery(id+"F0.wireOp",EDGE,"E72"),sQuery(id+"F0.wireOp",EDGE,"E75"),sQuery(id+"F0.wireOp",EDGE,"E76"),sQuery(id+"F0.wireOp",EDGE,"E79"),sQuery(id+"F0.wireOp",EDGE,"E80"),sQuery(id+"F0.wireOp",EDGE,"E81"),sQuery(id+"F0.wireOp",EDGE,"E82"),sQuery(id+"F0.wireOp",EDGE,"E84"),sQuery(id+"F0.wireOp",EDGE,"E85.0.MirrorCS"),sQuery(id+"F0.wireOp",EDGE,"E86.0.MirrorCS"),sQuery(id+"F0.wireOp",EDGE,"E87.0.MirrorCS"),sQuery(id+"F0.wireOp",EDGE,"E88.0.MirrorCS"),sQuery(id+"F0.wireOp",EDGE,"E89.0.MirrorCS"),sQuery(id+"F0.wireOp",EDGE,"E90.0.MirrorCS"),sQuery(id+"F0.wireOp",EDGE,"E91.0.MirrorCS"),sQuery(id+"F0.wireOp",EDGE,"E92.0.MirrorCS"),sQuery(id+"F0.wireOp",EDGE,"E93.0.MirrorCS"),sQuery(id+"F0.wireOp",EDGE,"E95"),sQuery(id+"F0.wireOp",EDGE,"E96"),sQuery(id+"F0.wireOp",EDGE,"E97"),sQuery(id+"F0.wireOp",EDGE,"E98"),sQuery(id+"F0.wireOp",EDGE,"E99"),sQuery(id+"F0.wireOp",EDGE,"E100"),sQuery(id+"F0.wireOp",EDGE,"E101"),sQuery(id+"F0.wireOp",EDGE,"E102"),sQuery(id+"F0.wireOp",EDGE,"E103"),sQuery(id+"F0.wireOp",EDGE,"E104"),sQuery(id+"F0.wireOp",EDGE,"E105.trimOffspring"),sQuery(id+"F0.wireOp",EDGE,"E106.trimOffspring"),sQuery(id+"F0.wireOp",EDGE,"E107.0.MirrorCS"),sQuery(id+"F0.wireOp",EDGE,"E107.1.MirrorCS"),sQuery(id+"F0.wireOp",EDGE,"E107.2.MirrorCS"),sQuery(id+"F0.wireOp",EDGE,"E107.3.MirrorCS"),sQuery(id+"F0.wireOp",EDGE,"E107.4.MirrorCS"),sQuery(id+"F0.wireOp",EDGE,"E107.5.MirrorCS"),sQuery(id+"F0.wireOp",EDGE,"E107.6.MirrorCS"),sQuery(id+"F0.wireOp",EDGE,"E107.7.MirrorCS"),sQuery(id+"F0.wireOp",EDGE,"E107.8.MirrorCS"),sQuery(id+"F0.wireOp",EDGE,"E107.9.MirrorCS"),sQuery(id+"F0.wireOp",EDGE,"E107.10.MirrorCS"),sQuery(id+"F0.wireOp",EDGE,"E107.11.MirrorCS"),sQuery(id+"F0.wireOp",EDGE,"E107.12.MirrorCS"),sQuery(id+"F0.wireOp",EDGE,"E107.13.MirrorCS"),sQuery(id+"F0.wireOp",EDGE,"E108"),sQuery(id+"F0.wireOp",EDGE,"E109"),sQuery(id+"F0.wireOp",EDGE,"E110"),sQuery(id+"F0.wireOp",EDGE,"E111"),sQuery(id+"F0.wireOp",EDGE,"E113.0.MirrorCS"),sQuery(id+"F0.wireOp",EDGE,"E114.0.MirrorCS"),sQuery(id+"F0.wireOp",EDGE,"E115.trimOffspring"),sQuery(id+"F0.wireOp",EDGE,"E116.0.MirrorCS"),sQuery(id+"F0.wireOp",EDGE,"E116.1.MirrorCS"),sQuery(id+"F0.wireOp",EDGE,"E116.2.MirrorCS"),sQuery(id+"F0.wireOp",EDGE,"E116.3.MirrorCS"),sQuery(id+"F0.wireOp",EDGE,"E116.4.MirrorCS"),sQuery(id+"F0.wireOp",EDGE,"E116.5.MirrorCS"),sQuery(id+"F0.wireOp",EDGE,"E116.6.MirrorCS"),sQuery(id+"F0.wireOp",EDGE,"E116.7.MirrorCS"),sQuery(id+"F0.wireOp",EDGE,"E116.8.MirrorCS"),sQuery(id+"F0.wireOp",EDGE,"E116.9.MirrorCS"),sQuery(id+"F0.wireOp",EDGE,"E116.10.MirrorCS"),sQuery(id+"F0.wireOp",EDGE,"E116.11.MirrorCS"),sQuery(id+"F0.wireOp",EDGE,"E116.12.MirrorCS"),sQuery(id+"F0.wireOp",EDGE,"E116.13.MirrorCS"),sQuery(id+"F0.wireOp",EDGE,"E116.14.MirrorCS"),sQuery(id+"F0.wireOp",EDGE,"E116.15.MirrorCS"),sQuery(id+"F0.wireOp",EDGE,"E116.16.MirrorCS"),sQuery(id+"F0.wireOp",EDGE,"E116.17.MirrorCS"),sQuery(id+"F0.wireOp",EDGE,"E116.18.MirrorCS"),sQuery(id+"F0.wireOp",EDGE,"E116.19.MirrorCS")])],"isStart":false});
            var sketch = newSketch(context, id + "F2", { "sketchPlane" : qUnion([Q0])});
            skPoint(sketch, "E117", {"position": v(39.05, 66.04) * mm});
            skLineSegment(sketch, "E118.rect.bottom", {"start": v(42.23, 62.87) * mm, "end": v(35.88, 62.87) * mm, "construction": true});
            skLineSegment(sketch, "E118.rect.top", {"start": v(42.23, 69.22) * mm, "end": v(35.88, 69.22) * mm, "construction": true});
            skLineSegment(sketch, "E118.rect.left", {"start": v(42.23, 62.87) * mm, "end": v(42.23, 69.22) * mm, "construction": true});
            skLineSegment(sketch, "E118.rect.right", {"start": v(35.88, 62.87) * mm, "end": v(35.88, 69.22) * mm, "construction": true});
            skLineSegment(sketch, "E119.bottom", {"start": v(42.23, 69.22) * mm, "end": v(45.4, 69.22) * mm});
            skLineSegment(sketch, "E119.top", {"start": v(42.23, 72.4) * mm, "end": v(45.4, 72.4) * mm});
            skLineSegment(sketch, "E119.left", {"start": v(42.23, 69.22) * mm, "end": v(42.23, 72.4) * mm});
            skLineSegment(sketch, "E119.right", {"start": v(45.4, 69.22) * mm, "end": v(45.4, 72.4) * mm});
            skLineSegment(sketch, "E120", {"start": v(35.88, 66.04) * mm, "end": v(42.23, 66.04) * mm, "construction": true});
            skLineSegment(sketch, "E121", {"start": v(39.05, 69.22) * mm, "end": v(39.05, 62.87) * mm, "construction": true});
            skLineSegment(sketch, "E122.0.MirrorCS", {"start": v(35.88, 69.22) * mm, "end": v(32.7, 69.22) * mm});
            skLineSegment(sketch, "E123.0.MirrorCS", {"start": v(32.7, 69.22) * mm, "end": v(32.7, 72.4) * mm});
            skLineSegment(sketch, "E124.0.MirrorCS", {"start": v(35.88, 72.4) * mm, "end": v(32.7, 72.4) * mm});
            skLineSegment(sketch, "E125.0.MirrorCS", {"start": v(35.88, 69.22) * mm, "end": v(35.88, 72.4) * mm});
            skLineSegment(sketch, "E126.0.MirrorCS", {"start": v(32.7, 62.87) * mm, "end": v(32.7, 59.7) * mm});
            skLineSegment(sketch, "E127.0.MirrorCS", {"start": v(35.88, 59.7) * mm, "end": v(32.7, 59.7) * mm});
            skLineSegment(sketch, "E128.0.MirrorCS", {"start": v(35.88, 62.87) * mm, "end": v(35.88, 59.7) * mm});
            skLineSegment(sketch, "E129.0.MirrorCS", {"start": v(42.23, 62.87) * mm, "end": v(45.4, 62.87) * mm});
            skLineSegment(sketch, "E130.0.MirrorCS", {"start": v(42.23, 62.87) * mm, "end": v(42.23, 59.7) * mm});
            skLineSegment(sketch, "E131.0.MirrorCS", {"start": v(42.23, 59.7) * mm, "end": v(45.4, 59.7) * mm});
            skLineSegment(sketch, "E132.0.MirrorCS", {"start": v(45.4, 62.87) * mm, "end": v(45.4, 59.7) * mm});
            skLineSegment(sketch, "E133.0.MirrorCS", {"start": v(35.88, 62.87) * mm, "end": v(32.7, 62.87) * mm});
            skLineSegment(sketch, "E134.0.MirrorCS", {"start": v(42.23, -69.21) * mm, "end": v(45.4, -69.21) * mm});
            skLineSegment(sketch, "E135.0.MirrorCS", {"start": v(45.4, -69.21) * mm, "end": v(45.4, -72.39) * mm});
            skLineSegment(sketch, "E136.0.MirrorCS", {"start": v(42.23, -72.39) * mm, "end": v(45.4, -72.39) * mm});
            skLineSegment(sketch, "E137.0.MirrorCS", {"start": v(42.23, -69.21) * mm, "end": v(42.23, -72.39) * mm});
            skLineSegment(sketch, "E138.0.MirrorCS", {"start": v(35.88, -69.21) * mm, "end": v(35.88, -72.39) * mm});
            skLineSegment(sketch, "E139.0.MirrorCS", {"start": v(35.88, -72.39) * mm, "end": v(32.7, -72.39) * mm});
            skLineSegment(sketch, "E140.0.MirrorCS", {"start": v(35.88, -69.21) * mm, "end": v(32.7, -69.21) * mm});
            skLineSegment(sketch, "E141.0.MirrorCS", {"start": v(32.7, -69.21) * mm, "end": v(32.7, -72.39) * mm});
            skLineSegment(sketch, "E142.0.MirrorCS", {"start": v(35.88, -62.86) * mm, "end": v(32.7, -62.86) * mm});
            skLineSegment(sketch, "E143.0.MirrorCS", {"start": v(35.88, -62.86) * mm, "end": v(35.88, -59.69) * mm});
            skLineSegment(sketch, "E144.0.MirrorCS", {"start": v(35.88, -59.69) * mm, "end": v(32.7, -59.69) * mm});
            skLineSegment(sketch, "E145.0.MirrorCS", {"start": v(32.7, -62.86) * mm, "end": v(32.7, -59.69) * mm});
            skLineSegment(sketch, "E146.0.MirrorCS", {"start": v(42.23, -62.86) * mm, "end": v(45.4, -62.86) * mm});
            skLineSegment(sketch, "E147.0.MirrorCS", {"start": v(42.23, -62.86) * mm, "end": v(42.23, -59.69) * mm});
            skLineSegment(sketch, "E148.0.MirrorCS", {"start": v(42.23, -59.69) * mm, "end": v(45.4, -59.69) * mm});
            skLineSegment(sketch, "E149.0.MirrorCS", {"start": v(45.4, -62.86) * mm, "end": v(45.4, -59.69) * mm});
            skPoint(sketch, "E150", {"position": v(39.05, 27.94) * mm});
            skLineSegment(sketch, "E151.rect.bottom", {"start": v(40.64, 29.65) * mm, "end": v(37.46, 29.65) * mm, "construction": true});
            skLineSegment(sketch, "E151.rect.top", {"start": v(40.64, 32.83) * mm, "end": v(37.46, 32.83) * mm, "construction": true});
            skLineSegment(sketch, "E151.rect.left", {"start": v(40.64, 29.65) * mm, "end": v(40.64, 32.83) * mm, "construction": true});
            skLineSegment(sketch, "E151.rect.right", {"start": v(37.46, 29.65) * mm, "end": v(37.46, 32.83) * mm, "construction": true});
            skPoint(sketch, "E151.rect.middle", {"position": v(39.05, 31.24) * mm});
            skLineSegment(sketch, "E152.rect.bottom", {"start": v(40.64, 23.05) * mm, "end": v(37.46, 23.05) * mm, "construction": true});
            skLineSegment(sketch, "E152.rect.top", {"start": v(40.64, 26.23) * mm, "end": v(37.46, 26.23) * mm, "construction": true});
            skLineSegment(sketch, "E152.rect.left", {"start": v(40.64, 23.05) * mm, "end": v(40.64, 26.23) * mm, "construction": true});
            skLineSegment(sketch, "E152.rect.right", {"start": v(37.46, 23.05) * mm, "end": v(37.46, 26.23) * mm, "construction": true});
            skPoint(sketch, "E152.rect.middle", {"position": v(39.05, 24.64) * mm});
            skLineSegment(sketch, "E153.0.MirrorCS", {"start": v(40.64, -26.23) * mm, "end": v(37.46, -26.23) * mm, "construction": true});
            skLineSegment(sketch, "E153.1.MirrorCS", {"start": v(40.64, -32.83) * mm, "end": v(37.46, -32.83) * mm, "construction": true});
            skLineSegment(sketch, "E153.2.MirrorCS", {"start": v(40.64, -29.65) * mm, "end": v(40.64, -32.83) * mm, "construction": true});
            skPoint(sketch, "E153.3.MirrorP", {"position": v(39.05, -31.24) * mm});
            skLineSegment(sketch, "E153.4.MirrorCS", {"start": v(37.46, -29.65) * mm, "end": v(37.46, -32.83) * mm, "construction": true});
            skLineSegment(sketch, "E153.5.MirrorCS", {"start": v(40.64, -29.65) * mm, "end": v(37.46, -29.65) * mm, "construction": true});
            skPoint(sketch, "E153.6.MirrorP", {"position": v(39.05, -27.94) * mm});
            skLineSegment(sketch, "E153.7.MirrorCS", {"start": v(40.64, -23.05) * mm, "end": v(40.64, -26.23) * mm, "construction": true});
            skPoint(sketch, "E153.8.MirrorP", {"position": v(39.05, -24.64) * mm});
            skLineSegment(sketch, "E153.9.MirrorCS", {"start": v(40.64, -23.05) * mm, "end": v(37.46, -23.05) * mm, "construction": true});
            skLineSegment(sketch, "E153.10.MirrorCS", {"start": v(37.46, -23.05) * mm, "end": v(37.46, -26.23) * mm, "construction": true});
            skPoint(sketch, "E154", {"position": v(-43.5, 66.04) * mm});
            skLineSegment(sketch, "E155.rect.bottom", {"start": v(-38.6, 64.45) * mm, "end": v(-41.78, 64.45) * mm});
            skLineSegment(sketch, "E155.rect.top", {"start": v(-38.6, 67.63) * mm, "end": v(-41.78, 67.63) * mm});
            skLineSegment(sketch, "E155.rect.left", {"start": v(-38.6, 64.45) * mm, "end": v(-38.6, 67.63) * mm});
            skLineSegment(sketch, "E155.rect.right", {"start": v(-41.78, 64.45) * mm, "end": v(-41.78, 67.63) * mm});
            skPoint(sketch, "E155.rect.middle", {"position": v(-40.2, 66.04) * mm});
            skLineSegment(sketch, "E156.rect.bottom", {"start": v(-45.21, 64.45) * mm, "end": v(-48.39, 64.45) * mm});
            skLineSegment(sketch, "E156.rect.top", {"start": v(-45.21, 67.63) * mm, "end": v(-48.39, 67.63) * mm});
            skLineSegment(sketch, "E156.rect.left", {"start": v(-45.21, 64.45) * mm, "end": v(-45.21, 67.63) * mm});
            skLineSegment(sketch, "E156.rect.right", {"start": v(-48.39, 64.45) * mm, "end": v(-48.39, 67.63) * mm});
            skPoint(sketch, "E156.rect.middle", {"position": v(-46.8, 66.04) * mm});
            skLineSegment(sketch, "E157.0.MirrorCS", {"start": v(-45.21, -67.63) * mm, "end": v(-48.39, -67.63) * mm});
            skPoint(sketch, "E157.1.MirrorP", {"position": v(-46.8, -66.04) * mm});
            skLineSegment(sketch, "E157.2.MirrorCS", {"start": v(-45.21, -64.45) * mm, "end": v(-45.21, -67.63) * mm});
            skPoint(sketch, "E157.3.MirrorP", {"position": v(-43.5, -66.04) * mm});
            skLineSegment(sketch, "E157.4.MirrorCS", {"start": v(-48.39, -64.45) * mm, "end": v(-48.39, -67.63) * mm});
            skLineSegment(sketch, "E157.5.MirrorCS", {"start": v(-45.21, -64.45) * mm, "end": v(-48.39, -64.45) * mm});
            skLineSegment(sketch, "E157.6.MirrorCS", {"start": v(-38.6, -67.63) * mm, "end": v(-41.78, -67.63) * mm});
            skLineSegment(sketch, "E157.7.MirrorCS", {"start": v(-41.78, -64.45) * mm, "end": v(-41.78, -67.63) * mm});
            skPoint(sketch, "E157.8.MirrorP", {"position": v(-40.2, -66.04) * mm});
            skLineSegment(sketch, "E157.9.MirrorCS", {"start": v(-38.6, -64.45) * mm, "end": v(-41.78, -64.45) * mm});
            skLineSegment(sketch, "E157.10.MirrorCS", {"start": v(-38.6, -64.45) * mm, "end": v(-38.6, -67.63) * mm});
            skSolve(sketch);
        }
        {
            var Q0;
            {Q0=qUnion([makeQuery(id+"F2.imprint","IMPRINT",FACE,{"disambiguationData":[TD([[makeQuery(id+"F2.imprint","IMPRINT",EDGE,{"derivedFrom":sQuery(id+"F2.wireOp",EDGE,"E119.bottom")}),1.0]])]}),makeQuery(id+"F2.imprint","IMPRINT",FACE,{"disambiguationData":[TD([[makeQuery(id+"F2.imprint","IMPRINT",EDGE,{"derivedFrom":sQuery(id+"F2.wireOp",EDGE,"E122.0.MirrorCS")}),-1.0]])]}),makeQuery(id+"F2.imprint","IMPRINT",FACE,{"disambiguationData":[TD([[makeQuery(id+"F2.imprint","IMPRINT",EDGE,{"derivedFrom":sQuery(id+"F2.wireOp",EDGE,"E126.0.MirrorCS")}),1.0]])]}),makeQuery(id+"F2.imprint","IMPRINT",FACE,{"disambiguationData":[TD([[makeQuery(id+"F2.imprint","IMPRINT",EDGE,{"derivedFrom":sQuery(id+"F2.wireOp",EDGE,"E129.0.MirrorCS")}),-1.0]])]}),makeQuery(id+"F2.imprint","IMPRINT",FACE,{"disambiguationData":[TD([[makeQuery(id+"F2.imprint","IMPRINT",EDGE,{"derivedFrom":sQuery(id+"F2.wireOp",EDGE,"E134.0.MirrorCS")}),-1.0]])]}),makeQuery(id+"F2.imprint","IMPRINT",FACE,{"disambiguationData":[TD([[makeQuery(id+"F2.imprint","IMPRINT",EDGE,{"derivedFrom":sQuery(id+"F2.wireOp",EDGE,"E138.0.MirrorCS")}),-1.0]])]}),makeQuery(id+"F2.imprint","IMPRINT",FACE,{"disambiguationData":[TD([[makeQuery(id+"F2.imprint","IMPRINT",EDGE,{"derivedFrom":sQuery(id+"F2.wireOp",EDGE,"E142.0.MirrorCS")}),-1.0]])]}),makeQuery(id+"F2.imprint","IMPRINT",FACE,{"disambiguationData":[TD([[makeQuery(id+"F2.imprint","IMPRINT",EDGE,{"derivedFrom":sQuery(id+"F2.wireOp",EDGE,"E146.0.MirrorCS")}),1.0]])]}),makeQuery(id+"F2.imprint","IMPRINT",FACE,{"disambiguationData":[TD([[makeQuery(id+"F2.imprint","IMPRINT",EDGE,{"derivedFrom":sQuery(id+"F2.wireOp",EDGE,"E155.rect.bottom")}),-1.0]])]}),makeQuery(id+"F2.imprint","IMPRINT",FACE,{"disambiguationData":[TD([[makeQuery(id+"F2.imprint","IMPRINT",EDGE,{"derivedFrom":sQuery(id+"F2.wireOp",EDGE,"E156.rect.bottom")}),-1.0]])]}),makeQuery(id+"F2.imprint","IMPRINT",FACE,{"disambiguationData":[TD([[makeQuery(id+"F2.imprint","IMPRINT",EDGE,{"derivedFrom":sQuery(id+"F2.wireOp",EDGE,"E157.0.MirrorCS")}),-1.0]])]}),makeQuery(id+"F2.imprint","IMPRINT",FACE,{"disambiguationData":[TD([[makeQuery(id+"F2.imprint","IMPRINT",EDGE,{"derivedFrom":sQuery(id+"F2.wireOp",EDGE,"E157.6.MirrorCS")}),-1.0]])]})]);}
            var Q1;
            Q1=makeQuery(id+"F1.opExtrude","CAP_FACE",FACE,{"disambiguationData":[OSD([sQuery(id+"F0.wireOp",EDGE,"E2"),sQuery(id+"F0.wireOp",EDGE,"E3"),sQuery(id+"F0.wireOp",EDGE,"E4"),sQuery(id+"F0.wireOp",EDGE,"E5"),sQuery(id+"F0.wireOp",EDGE,"E6.rect.bottom"),sQuery(id+"F0.wireOp",EDGE,"E6.rect.top"),sQuery(id+"F0.wireOp",EDGE,"E6.rect.left"),sQuery(id+"F0.wireOp",EDGE,"E6.rect.right"),sQuery(id+"F0.wireOp",EDGE,"E8.rect.bottom"),sQuery(id+"F0.wireOp",EDGE,"E8.rect.top"),sQuery(id+"F0.wireOp",EDGE,"E8.rect.left"),sQuery(id+"F0.wireOp",EDGE,"E8.rect.right"),sQuery(id+"F0.wireOp",EDGE,"E9.1.MirrorCS"),sQuery(id+"F0.wireOp",EDGE,"E10.0.MirrorCS"),sQuery(id+"F0.wireOp",EDGE,"E11.0.MirrorCS"),sQuery(id+"F0.wireOp",EDGE,"E12.0.MirrorCS"),sQuery(id+"F0.wireOp",EDGE,"E14"),sQuery(id+"F0.wireOp",EDGE,"E17.0.MirrorCS"),sQuery(id+"F0.wireOp",EDGE,"E19.bottom"),sQuery(id+"F0.wireOp",EDGE,"E19.top"),sQuery(id+"F0.wireOp",EDGE,"E19.left"),sQuery(id+"F0.wireOp",EDGE,"E19.right"),sQuery(id+"F0.wireOp",EDGE,"E20"),sQuery(id+"F0.wireOp",EDGE,"E21.0.MirrorC"),sQuery(id+"F0.wireOp",EDGE,"E26"),sQuery(id+"F0.wireOp",EDGE,"E27"),sQuery(id+"F0.wireOp",EDGE,"E28"),sQuery(id+"F0.wireOp",EDGE,"E29"),sQuery(id+"F0.wireOp",EDGE,"E30.0.MirrorC"),sQuery(id+"F0.wireOp",EDGE,"E31.0.MirrorC"),sQuery(id+"F0.wireOp",EDGE,"E32.0.MirrorC"),sQuery(id+"F0.wireOp",EDGE,"E33.0.MirrorC"),sQuery(id+"F0.wireOp",EDGE,"E34.0.MirrorC"),sQuery(id+"F0.wireOp",EDGE,"E34.1.MirrorC"),sQuery(id+"F0.wireOp",EDGE,"E34.2.MirrorC"),sQuery(id+"F0.wireOp",EDGE,"E34.3.MirrorC"),sQuery(id+"F0.wireOp",EDGE,"E35.0.MirrorC"),sQuery(id+"F0.wireOp",EDGE,"E36.0.MirrorC"),sQuery(id+"F0.wireOp",EDGE,"E37.0.MirrorC"),sQuery(id+"F0.wireOp",EDGE,"E38.0.MirrorC"),sQuery(id+"F0.wireOp",EDGE,"E39.0.MirrorCS"),sQuery(id+"F0.wireOp",EDGE,"E39.1.MirrorCS"),sQuery(id+"F0.wireOp",EDGE,"E39.2.MirrorCS"),sQuery(id+"F0.wireOp",EDGE,"E39.3.MirrorCS"),sQuery(id+"F0.wireOp",EDGE,"E39.4.MirrorCS"),sQuery(id+"F0.wireOp",EDGE,"E39.5.MirrorCS"),sQuery(id+"F0.wireOp",EDGE,"E39.6.MirrorCS"),sQuery(id+"F0.wireOp",EDGE,"E39.7.MirrorCS"),sQuery(id+"F0.wireOp",EDGE,"E39.8.MirrorCS"),sQuery(id+"F0.wireOp",EDGE,"E39.9.MirrorCS"),sQuery(id+"F0.wireOp",EDGE,"E39.10.MirrorCS"),sQuery(id+"F0.wireOp",EDGE,"E39.11.MirrorCS"),sQuery(id+"F0.wireOp",EDGE,"E39.12.MirrorCS"),sQuery(id+"F0.wireOp",EDGE,"E39.13.MirrorCS"),sQuery(id+"F0.wireOp",EDGE,"E39.15.MirrorCS"),sQuery(id+"F0.wireOp",EDGE,"E39.16.MirrorCS"),sQuery(id+"F0.wireOp",EDGE,"E39.17.MirrorCS"),sQuery(id+"F0.wireOp",EDGE,"E39.18.MirrorCS"),sQuery(id+"F0.wireOp",EDGE,"E39.19.MirrorCS"),sQuery(id+"F0.wireOp",EDGE,"E39.21.MirrorCS"),sQuery(id+"F0.wireOp",EDGE,"E41.rect.left"),sQuery(id+"F0.wireOp",EDGE,"E41.rect.right"),sQuery(id+"F0.wireOp",EDGE,"E42"),sQuery(id+"F0.wireOp",EDGE,"E43"),sQuery(id+"F0.wireOp",EDGE,"E44"),sQuery(id+"F0.wireOp",EDGE,"E45"),sQuery(id+"F0.wireOp",EDGE,"E46.trimOffspring"),sQuery(id+"F0.wireOp",EDGE,"E47.trimOffspring"),sQuery(id+"F0.wireOp",EDGE,"E48"),sQuery(id+"F0.wireOp",EDGE,"E49"),sQuery(id+"F0.wireOp",EDGE,"E50"),sQuery(id+"F0.wireOp",EDGE,"E51"),sQuery(id+"F0.wireOp",EDGE,"E52"),sQuery(id+"F0.wireOp",EDGE,"E53"),sQuery(id+"F0.wireOp",EDGE,"E54.trimOffspring"),sQuery(id+"F0.wireOp",EDGE,"E55.trimOffspring"),sQuery(id+"F0.wireOp",EDGE,"E56.1.MirrorCS"),sQuery(id+"F0.wireOp",EDGE,"E56.2.MirrorCS"),sQuery(id+"F0.wireOp",EDGE,"E56.3.MirrorCS"),sQuery(id+"F0.wireOp",EDGE,"E56.4.MirrorCS"),sQuery(id+"F0.wireOp",EDGE,"E56.5.MirrorCS"),sQuery(id+"F0.wireOp",EDGE,"E56.6.MirrorCS"),sQuery(id+"F0.wireOp",EDGE,"E56.7.MirrorCS"),sQuery(id+"F0.wireOp",EDGE,"E56.8.MirrorCS"),sQuery(id+"F0.wireOp",EDGE,"E56.9.MirrorCS"),sQuery(id+"F0.wireOp",EDGE,"E56.10.MirrorCS"),sQuery(id+"F0.wireOp",EDGE,"E56.11.MirrorCS"),sQuery(id+"F0.wireOp",EDGE,"E56.12.MirrorCS"),sQuery(id+"F0.wireOp",EDGE,"E56.13.MirrorCS"),sQuery(id+"F0.wireOp",EDGE,"E56.14.MirrorCS"),sQuery(id+"F0.wireOp",EDGE,"E56.15.MirrorCS"),sQuery(id+"F0.wireOp",EDGE,"E56.16.MirrorCS"),sQuery(id+"F0.wireOp",EDGE,"E56.17.MirrorCS"),sQuery(id+"F0.wireOp",EDGE,"E56.18.MirrorCS"),sQuery(id+"F0.wireOp",EDGE,"E56.19.MirrorCS"),sQuery(id+"F0.wireOp",EDGE,"E56.20.MirrorCS"),sQuery(id+"F0.wireOp",EDGE,"E57.rect.left"),sQuery(id+"F0.wireOp",EDGE,"E57.rect.right"),sQuery(id+"F0.wireOp",EDGE,"E58"),sQuery(id+"F0.wireOp",EDGE,"E59"),sQuery(id+"F0.wireOp",EDGE,"E60"),sQuery(id+"F0.wireOp",EDGE,"E61"),sQuery(id+"F0.wireOp",EDGE,"E62.trimOffspring"),sQuery(id+"F0.wireOp",EDGE,"E57.rect.bottom"),sQuery(id+"F0.wireOp",EDGE,"E63"),sQuery(id+"F0.wireOp",EDGE,"E64"),sQuery(id+"F0.wireOp",EDGE,"E65"),sQuery(id+"F0.wireOp",EDGE,"E66.0.MirrorCS"),sQuery(id+"F0.wireOp",EDGE,"E66.1.MirrorCS"),sQuery(id+"F0.wireOp",EDGE,"E66.2.MirrorCS"),sQuery(id+"F0.wireOp",EDGE,"E67.trimOffspring"),sQuery(id+"F0.wireOp",EDGE,"E68.trimOffspring"),sQuery(id+"F0.wireOp",EDGE,"E69.1.MirrorCS"),sQuery(id+"F0.wireOp",EDGE,"E69.2.MirrorCS"),sQuery(id+"F0.wireOp",EDGE,"E69.3.MirrorCS"),sQuery(id+"F0.wireOp",EDGE,"E69.4.MirrorCS"),sQuery(id+"F0.wireOp",EDGE,"E69.5.MirrorCS"),sQuery(id+"F0.wireOp",EDGE,"E69.7.MirrorCS"),sQuery(id+"F0.wireOp",EDGE,"E69.8.MirrorCS"),sQuery(id+"F0.wireOp",EDGE,"E69.9.MirrorCS"),sQuery(id+"F0.wireOp",EDGE,"E69.11.MirrorCS"),sQuery(id+"F0.wireOp",EDGE,"E69.12.MirrorCS"),sQuery(id+"F0.wireOp",EDGE,"E69.13.MirrorCS"),sQuery(id+"F0.wireOp",EDGE,"E69.14.MirrorCS"),sQuery(id+"F0.wireOp",EDGE,"E69.15.MirrorCS"),sQuery(id+"F0.wireOp",EDGE,"E69.16.MirrorCS"),sQuery(id+"F0.wireOp",EDGE,"E69.17.MirrorCS"),sQuery(id+"F0.wireOp",EDGE,"E69.18.MirrorCS"),sQuery(id+"F0.wireOp",EDGE,"E69.19.MirrorCS"),sQuery(id+"F0.wireOp",EDGE,"E69.20.MirrorCS"),sQuery(id+"F0.wireOp",EDGE,"E69.21.MirrorCS"),sQuery(id+"F0.wireOp",EDGE,"E69.22.MirrorCS"),sQuery(id+"F0.wireOp",EDGE,"E70"),sQuery(id+"F0.wireOp",EDGE,"E71"),sQuery(id+"F0.wireOp",EDGE,"E72"),sQuery(id+"F0.wireOp",EDGE,"E75"),sQuery(id+"F0.wireOp",EDGE,"E76"),sQuery(id+"F0.wireOp",EDGE,"E79"),sQuery(id+"F0.wireOp",EDGE,"E80"),sQuery(id+"F0.wireOp",EDGE,"E81"),sQuery(id+"F0.wireOp",EDGE,"E82"),sQuery(id+"F0.wireOp",EDGE,"E84"),sQuery(id+"F0.wireOp",EDGE,"E85.0.MirrorCS"),sQuery(id+"F0.wireOp",EDGE,"E86.0.MirrorCS"),sQuery(id+"F0.wireOp",EDGE,"E87.0.MirrorCS"),sQuery(id+"F0.wireOp",EDGE,"E88.0.MirrorCS"),sQuery(id+"F0.wireOp",EDGE,"E89.0.MirrorCS"),sQuery(id+"F0.wireOp",EDGE,"E90.0.MirrorCS"),sQuery(id+"F0.wireOp",EDGE,"E91.0.MirrorCS"),sQuery(id+"F0.wireOp",EDGE,"E92.0.MirrorCS"),sQuery(id+"F0.wireOp",EDGE,"E93.0.MirrorCS"),sQuery(id+"F0.wireOp",EDGE,"E95"),sQuery(id+"F0.wireOp",EDGE,"E96"),sQuery(id+"F0.wireOp",EDGE,"E97"),sQuery(id+"F0.wireOp",EDGE,"E98"),sQuery(id+"F0.wireOp",EDGE,"E99"),sQuery(id+"F0.wireOp",EDGE,"E100"),sQuery(id+"F0.wireOp",EDGE,"E101"),sQuery(id+"F0.wireOp",EDGE,"E102"),sQuery(id+"F0.wireOp",EDGE,"E103"),sQuery(id+"F0.wireOp",EDGE,"E104"),sQuery(id+"F0.wireOp",EDGE,"E105.trimOffspring"),sQuery(id+"F0.wireOp",EDGE,"E106.trimOffspring"),sQuery(id+"F0.wireOp",EDGE,"E107.0.MirrorCS"),sQuery(id+"F0.wireOp",EDGE,"E107.1.MirrorCS"),sQuery(id+"F0.wireOp",EDGE,"E107.2.MirrorCS"),sQuery(id+"F0.wireOp",EDGE,"E107.3.MirrorCS"),sQuery(id+"F0.wireOp",EDGE,"E107.4.MirrorCS"),sQuery(id+"F0.wireOp",EDGE,"E107.5.MirrorCS"),sQuery(id+"F0.wireOp",EDGE,"E107.6.MirrorCS"),sQuery(id+"F0.wireOp",EDGE,"E107.7.MirrorCS"),sQuery(id+"F0.wireOp",EDGE,"E107.8.MirrorCS"),sQuery(id+"F0.wireOp",EDGE,"E107.9.MirrorCS"),sQuery(id+"F0.wireOp",EDGE,"E107.10.MirrorCS"),sQuery(id+"F0.wireOp",EDGE,"E107.11.MirrorCS"),sQuery(id+"F0.wireOp",EDGE,"E107.12.MirrorCS"),sQuery(id+"F0.wireOp",EDGE,"E107.13.MirrorCS"),sQuery(id+"F0.wireOp",EDGE,"E108"),sQuery(id+"F0.wireOp",EDGE,"E109"),sQuery(id+"F0.wireOp",EDGE,"E110"),sQuery(id+"F0.wireOp",EDGE,"E111"),sQuery(id+"F0.wireOp",EDGE,"E113.0.MirrorCS"),sQuery(id+"F0.wireOp",EDGE,"E114.0.MirrorCS"),sQuery(id+"F0.wireOp",EDGE,"E115.trimOffspring"),sQuery(id+"F0.wireOp",EDGE,"E116.0.MirrorCS"),sQuery(id+"F0.wireOp",EDGE,"E116.1.MirrorCS"),sQuery(id+"F0.wireOp",EDGE,"E116.2.MirrorCS"),sQuery(id+"F0.wireOp",EDGE,"E116.3.MirrorCS"),sQuery(id+"F0.wireOp",EDGE,"E116.4.MirrorCS"),sQuery(id+"F0.wireOp",EDGE,"E116.5.MirrorCS"),sQuery(id+"F0.wireOp",EDGE,"E116.6.MirrorCS"),sQuery(id+"F0.wireOp",EDGE,"E116.7.MirrorCS"),sQuery(id+"F0.wireOp",EDGE,"E116.8.MirrorCS"),sQuery(id+"F0.wireOp",EDGE,"E116.9.MirrorCS"),sQuery(id+"F0.wireOp",EDGE,"E116.10.MirrorCS"),sQuery(id+"F0.wireOp",EDGE,"E116.11.MirrorCS"),sQuery(id+"F0.wireOp",EDGE,"E116.12.MirrorCS"),sQuery(id+"F0.wireOp",EDGE,"E116.13.MirrorCS"),sQuery(id+"F0.wireOp",EDGE,"E116.14.MirrorCS"),sQuery(id+"F0.wireOp",EDGE,"E116.15.MirrorCS"),sQuery(id+"F0.wireOp",EDGE,"E116.16.MirrorCS"),sQuery(id+"F0.wireOp",EDGE,"E116.17.MirrorCS"),sQuery(id+"F0.wireOp",EDGE,"E116.18.MirrorCS"),sQuery(id+"F0.wireOp",EDGE,"E116.19.MirrorCS")])],"isStart":true});
            extrude(context, id + "F3", {"entities" : qUnion([Q0]), "operationType" : NewBodyOperationType.REMOVE, "endBound" : BoundingType.UP_TO_SURFACE, "oppositeDirection" : true, "endBoundEntityFace" : qUnion([Q1]), "depth" : 25.4 * mm});
        }
    });
